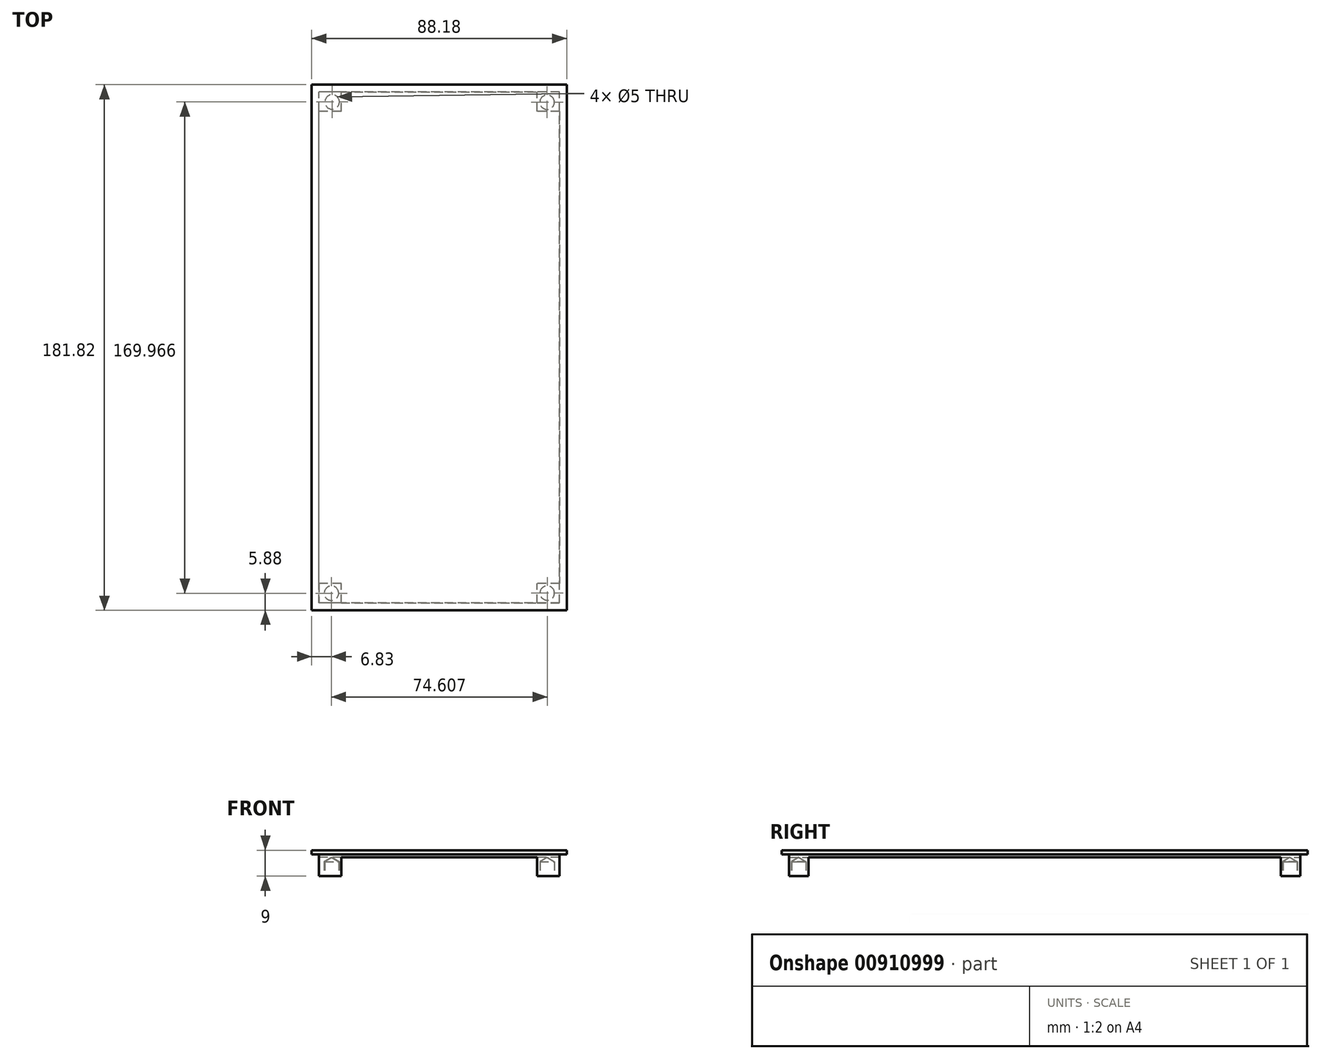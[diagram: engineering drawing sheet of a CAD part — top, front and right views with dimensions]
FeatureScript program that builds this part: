
annotation { "Feature Type Name" : "Feature", "Feature Type Description" : "" }
export const myFeature = defineFeature(function(context is Context, id is Id, definition is map)
    precondition{}
    {
        {
            var Q0;
            Q0=qCreatedBy(makeId("Top.planeOp"),FACE);
            var sketch = newSketch(context, id + "F0", { "sketchPlane" : qUnion([Q0])});
            skLineSegment(sketch, "E0.bottom", {"start": v(44.1, 90.91) * mm, "end": v(-44.1, 90.91) * mm});
            skLineSegment(sketch, "E0.top", {"start": v(44.1, -90.91) * mm, "end": v(-44.1, -90.91) * mm});
            skLineSegment(sketch, "E0.left", {"start": v(44.1, 90.91) * mm, "end": v(44.1, -90.91) * mm});
            skLineSegment(sketch, "E0.right", {"start": v(-44.1, 90.91) * mm, "end": v(-44.1, -90.91) * mm});
            skPoint(sketch, "E0.middle", {"position": v(0, 0) * mm});
            skSolve(sketch);
        }
        {
            var Q0;
            Q0=qSketchRegion(id+"F0",true);
            var Q1;
            Q1=sQuery(id+"F0.wireOp",EDGE,"E0.top");
            var Q2;
            Q2=sQuery(id+"F0.wireOp",EDGE,"E0.left");
            var Q3;
            Q3=sQuery(id+"F0.wireOp",EDGE,"E0.bottom");
            var Q4;
            Q4=sQuery(id+"F0.wireOp",EDGE,"E0.right");
            extrude(context, id + "F1", {"entities" : qUnion([Q0]), "surfaceEntities" : qUnion([Q1, Q2, Q3, Q4]), "depth" : 2.5 * mm, "offsetDistance" : 25 * mm});
        }
        {
            var Q0;
            Q0=qCreatedBy(makeId("Top.planeOp"),FACE);
            var sketch = newSketch(context, id + "F2", { "sketchPlane" : qUnion([Q0])});
            skLineSegment(sketch, "E1.bottom", {"start": v(44.09, -88.41) * mm, "end": v(-44.1, -88.41) * mm});
            skLineSegment(sketch, "E1.top", {"start": v(44.09, -90.92) * mm, "end": v(-44.1, -90.92) * mm});
            skLineSegment(sketch, "E1.left", {"start": v(44.09, -88.41) * mm, "end": v(44.09, -90.92) * mm});
            skLineSegment(sketch, "E1.right", {"start": v(-44.1, -88.41) * mm, "end": v(-44.1, -90.92) * mm});
            skSolve(sketch);
        }
        {
            var Q0;
            Q0=qSketchRegion(id+"F2",true);
            extrude(context, id + "F3", {"entities" : qUnion([Q0]), "operationType" : NewBodyOperationType.REMOVE, "depth" : 1 * mm, "offsetDistance" : 25 * mm});
        }
        {
            var Q0;
            Q0=makeQuery(id+"F1.opExtrude","CAP_FACE",FACE,{"disambiguationData":[OSD([sQuery(id+"F0.wireOp",EDGE,"E0.bottom"),sQuery(id+"F0.wireOp",EDGE,"E0.top"),sQuery(id+"F0.wireOp",EDGE,"E0.left"),sQuery(id+"F0.wireOp",EDGE,"E0.right")])],"isStart":true});
            var sketch = newSketch(context, id + "F4", { "sketchPlane" : qUnion([Q0])});
            skLineSegment(sketch, "E2.bottom", {"start": v(44.09, -88.4) * mm, "end": v(-44.1, -88.4) * mm});
            skLineSegment(sketch, "E2.top", {"start": v(44.09, -90.91) * mm, "end": v(-44.1, -90.91) * mm});
            skLineSegment(sketch, "E2.left", {"start": v(44.09, -88.4) * mm, "end": v(44.09, -90.91) * mm});
            skLineSegment(sketch, "E2.right", {"start": v(-44.1, -88.4) * mm, "end": v(-44.1, -90.91) * mm});
            skSolve(sketch);
        }
        {
            var Q0;
            Q0=qSketchRegion(id+"F4",true);
            extrude(context, id + "F5", {"entities" : qUnion([Q0]), "operationType" : NewBodyOperationType.REMOVE, "oppositeDirection" : true, "depth" : 1 * mm, "offsetDistance" : 25 * mm});
        }
        {
            var Q0;
            Q0=qCreatedBy(makeId("Top.planeOp"),FACE);
            var sketch = newSketch(context, id + "F6", { "sketchPlane" : qUnion([Q0])});
            skLineSegment(sketch, "E3.bottom", {"start": v(44.1, -90.92) * mm, "end": v(41.6, -90.92) * mm});
            skLineSegment(sketch, "E3.top", {"start": v(44.1, 90.91) * mm, "end": v(41.6, 90.91) * mm});
            skLineSegment(sketch, "E3.left", {"start": v(44.1, -90.92) * mm, "end": v(44.1, 90.91) * mm});
            skLineSegment(sketch, "E3.right", {"start": v(41.6, -90.92) * mm, "end": v(41.6, 90.91) * mm});
            skSolve(sketch);
        }
        {
            var Q0;
            Q0=qSketchRegion(id+"F6",true);
            extrude(context, id + "F7", {"entities" : qUnion([Q0]), "operationType" : NewBodyOperationType.REMOVE, "depth" : 1 * mm, "offsetDistance" : 25 * mm});
        }
        {
            var Q0;
            Q0=qCreatedBy(makeId("Top.planeOp"),FACE);
            var sketch = newSketch(context, id + "F8", { "sketchPlane" : qUnion([Q0])});
            skLineSegment(sketch, "E4.bottom", {"start": v(-41.6, -90.91) * mm, "end": v(-44.1, -90.91) * mm});
            skLineSegment(sketch, "E4.top", {"start": v(-41.6, 90.91) * mm, "end": v(-44.1, 90.91) * mm});
            skLineSegment(sketch, "E4.left", {"start": v(-41.6, -90.91) * mm, "end": v(-41.6, 90.91) * mm});
            skLineSegment(sketch, "E4.right", {"start": v(-44.1, -90.91) * mm, "end": v(-44.1, 90.91) * mm});
            skSolve(sketch);
        }
        {
            var Q0;
            Q0=qSketchRegion(id+"F8",true);
            extrude(context, id + "F9", {"entities" : qUnion([Q0]), "operationType" : NewBodyOperationType.REMOVE, "depth" : 1 * mm, "offsetDistance" : 25 * mm});
        }
        {
            var Q0;
            Q0=makeQuery(id+"F1.opExtrude","CAP_FACE",FACE,{"disambiguationData":[OSD([sQuery(id+"F0.wireOp",EDGE,"E0.bottom"),sQuery(id+"F0.wireOp",EDGE,"E0.top"),sQuery(id+"F0.wireOp",EDGE,"E0.left"),sQuery(id+"F0.wireOp",EDGE,"E0.right")])],"isStart":true});
            var sketch = newSketch(context, id + "F10", { "sketchPlane" : qUnion([Q0])});
            skLineSegment(sketch, "E5.bottom", {"start": v(41.6, -81.64) * mm, "end": v(33.89, -81.64) * mm});
            skLineSegment(sketch, "E5.top", {"start": v(41.6, -88.4) * mm, "end": v(33.89, -88.4) * mm});
            skLineSegment(sketch, "E5.left", {"start": v(41.6, -81.64) * mm, "end": v(41.6, -88.4) * mm});
            skLineSegment(sketch, "E5.right", {"start": v(33.89, -81.64) * mm, "end": v(33.89, -88.4) * mm});
            skLineSegment(sketch, "E6.bottom", {"start": v(-33.9, -81.64) * mm, "end": v(-41.6, -81.64) * mm});
            skLineSegment(sketch, "E6.top", {"start": v(-33.9, -88.4) * mm, "end": v(-41.6, -88.4) * mm});
            skLineSegment(sketch, "E6.left", {"start": v(-33.9, -81.64) * mm, "end": v(-33.9, -88.4) * mm});
            skLineSegment(sketch, "E6.right", {"start": v(-41.6, -81.64) * mm, "end": v(-41.6, -88.4) * mm});
            skLineSegment(sketch, "E7.bottom", {"start": v(-33.9, 88.41) * mm, "end": v(-41.6, 88.41) * mm});
            skLineSegment(sketch, "E7.top", {"start": v(-33.9, 81.65) * mm, "end": v(-41.6, 81.65) * mm});
            skLineSegment(sketch, "E7.left", {"start": v(-33.9, 88.41) * mm, "end": v(-33.9, 81.65) * mm});
            skLineSegment(sketch, "E7.right", {"start": v(-41.6, 88.41) * mm, "end": v(-41.6, 81.65) * mm});
            skLineSegment(sketch, "E8.bottom", {"start": v(41.6, 88.41) * mm, "end": v(33.89, 88.41) * mm});
            skLineSegment(sketch, "E8.top", {"start": v(41.6, 81.65) * mm, "end": v(33.89, 81.65) * mm});
            skLineSegment(sketch, "E8.left", {"start": v(41.6, 88.41) * mm, "end": v(41.6, 81.65) * mm});
            skLineSegment(sketch, "E8.right", {"start": v(33.89, 88.41) * mm, "end": v(33.89, 81.65) * mm});
            skSolve(sketch);
        }
        {
            var Q0;
            Q0=qSketchRegion(id+"F10",true);
            extrude(context, id + "F11", {"entities" : qUnion([Q0]), "operationType" : NewBodyOperationType.ADD, "depth" : 6.5 * mm, "offsetDistance" : 25 * mm});
        }
        {
            var Q0;
            Q0=makeQuery(id+"F11.opExtrude","CAP_FACE",FACE,{"disambiguationData":[OSD([sQuery(id+"F10.wireOp",EDGE,"E7.bottom"),sQuery(id+"F10.wireOp",EDGE,"E7.top"),sQuery(id+"F10.wireOp",EDGE,"E7.left"),sQuery(id+"F10.wireOp",EDGE,"E7.right")])],"isStart":false});
            var sketch = newSketch(context, id + "F12", { "sketchPlane" : qUnion([Q0])});
            skCircle(sketch, "E9", {"center": v(-37.26, 85.03) * mm, "radius": 2.37 * mm});
            skSolve(sketch);
        }
        {
            var Q0;
            Q0=makeQuery(id+"F11.opExtrude","CAP_FACE",FACE,{"disambiguationData":[OSD([sQuery(id+"F10.wireOp",EDGE,"E8.bottom"),sQuery(id+"F10.wireOp",EDGE,"E8.top"),sQuery(id+"F10.wireOp",EDGE,"E8.left"),sQuery(id+"F10.wireOp",EDGE,"E8.right")])],"isStart":false});
            var sketch = newSketch(context, id + "F13", { "sketchPlane" : qUnion([Q0])});
            skCircle(sketch, "E10", {"center": v(37.35, 84.96) * mm, "radius": 2.37 * mm});
            skSolve(sketch);
        }
        {
            var Q0;
            Q0=makeQuery(id+"F11.opExtrude","CAP_FACE",FACE,{"disambiguationData":[OSD([sQuery(id+"F10.wireOp",EDGE,"E5.bottom"),sQuery(id+"F10.wireOp",EDGE,"E5.top"),sQuery(id+"F10.wireOp",EDGE,"E5.left"),sQuery(id+"F10.wireOp",EDGE,"E5.right")])],"isStart":false});
            var sketch = newSketch(context, id + "F14", { "sketchPlane" : qUnion([Q0])});
            skCircle(sketch, "E11", {"center": v(37.32, -84.85) * mm, "radius": 2.37 * mm});
            skSolve(sketch);
        }
        {
            var Q0;
            Q0=makeQuery(id+"F11.opExtrude","CAP_FACE",FACE,{"disambiguationData":[OSD([sQuery(id+"F10.wireOp",EDGE,"E6.bottom"),sQuery(id+"F10.wireOp",EDGE,"E6.top"),sQuery(id+"F10.wireOp",EDGE,"E6.left"),sQuery(id+"F10.wireOp",EDGE,"E6.right")])],"isStart":false});
            var sketch = newSketch(context, id + "F15", { "sketchPlane" : qUnion([Q0])});
            skCircle(sketch, "E12", {"center": v(-37.02, -84.94) * mm, "radius": 2.37 * mm});
            skSolve(sketch);
        }
        {
            var Q0;
            Q0=sQuery(id+"F15.wireOp",VERTEX,"E12.center");
            var Q1;
            Q1=sQuery(id+"F14.wireOp",VERTEX,"E11.center");
            var Q2;
            Q2=sQuery(id+"F13.wireOp",VERTEX,"E10.center");
            var Q3;
            Q3=sQuery(id+"F12.wireOp",VERTEX,"E9.center");
            var Q4;
            Q4=makeQuery(id+"F1.opExtrude","SWEPT_BODY",BODY,{"disambiguationData":[OSD([sQuery(id+"F0.wireOp",EDGE,"E0.bottom"),sQuery(id+"F0.wireOp",EDGE,"E0.top"),sQuery(id+"F0.wireOp",EDGE,"E0.left"),sQuery(id+"F0.wireOp",EDGE,"E0.right")])]});
            hole(context, id + "F16", {"style" : HoleStyle.SIMPLE, "endStyle" : HoleEndStyle.BLIND, "holeDiameter" : 5 * mm, "majorDiameter" : 5 * mm, "holeDepth" : 5 * mm, "isTappedThrough" : true, "tappedDepth" : 12 * mm, "tapClearance" : 3, "locations" : qUnion([Q0, Q1, Q2, Q3]), "scope" : qUnion([Q4])});
        }
    });
